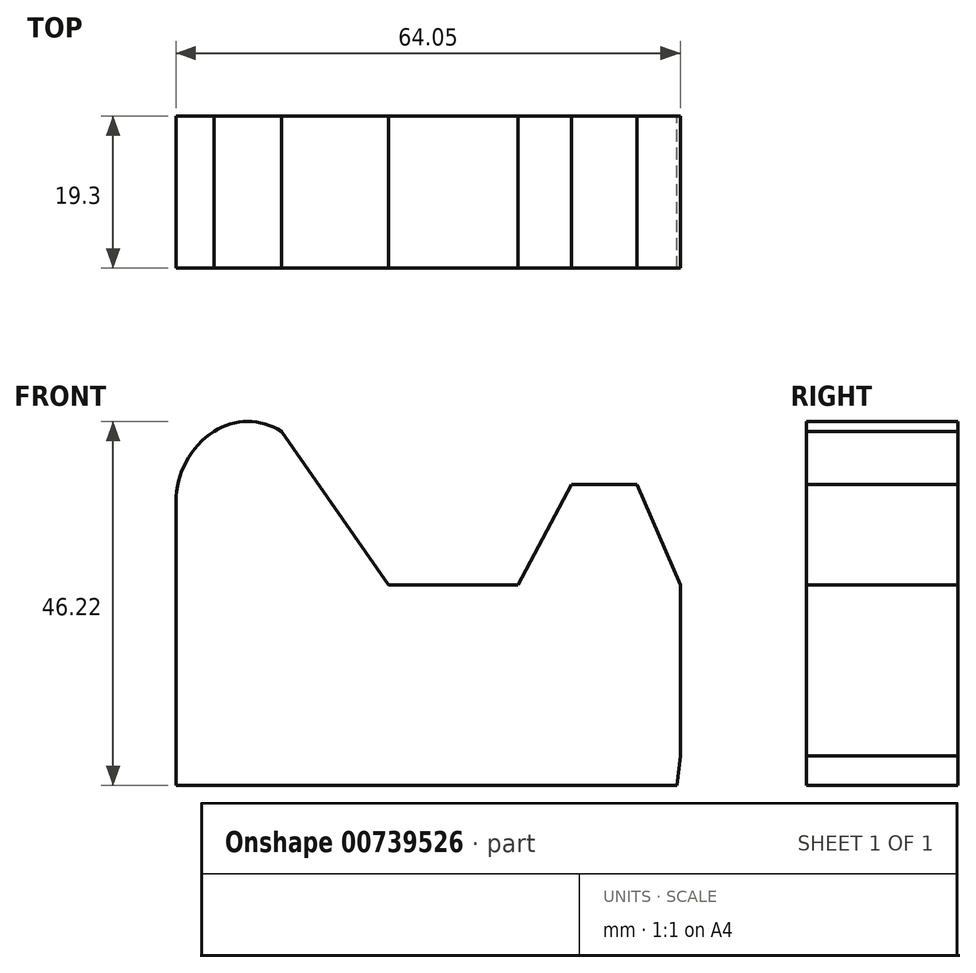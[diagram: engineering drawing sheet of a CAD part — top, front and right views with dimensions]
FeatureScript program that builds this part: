
annotation { "Feature Type Name" : "Feature", "Feature Type Description" : "" }
export const myFeature = defineFeature(function(context is Context, id is Id, definition is map)
    precondition{}
    {
        {
            var Q0;
            Q0=qCreatedBy(makeId("Front.planeOp"),FACE);
            var sketch = newSketch(context, id + "F0", { "sketchPlane" : qUnion([Q0])});
            skLineSegment(sketch, "E0.bottom", {"start": v(-26.99, 1.9) * mm, "end": v(26.99, 1.9) * mm});
            skLineSegment(sketch, "E0.top", {"start": v(-26.99, -1.9) * mm, "end": v(26.99, -1.9) * mm});
            skLineSegment(sketch, "E0.left", {"start": v(-26.99, 1.9) * mm, "end": v(-26.99, -1.9) * mm});
            skPoint(sketch, "E0.middle", {"position": v(0, 0) * mm});
            skLineSegment(sketch, "E1", {"start": v(-26.99, 1.9) * mm, "end": v(-26.99, 34.11) * mm});
            skArc(sketch, "E2", {"start": v(-22.18, 43.08) * mm, "mid": v(-25.7, 39.2) * mm, "end": v(-26.99, 34.11) * mm});
            skArc(sketch, "E3", {"start": v(-13.6, 43.08) * mm, "mid": v(-17.9, 44.32) * mm, "end": v(-22.18, 43.08) * mm});
            skLineSegment(sketch, "E4", {"start": v(-13.6, 43.08) * mm, "end": v(0, 23.58) * mm});
            skLineSegment(sketch, "E5", {"start": v(0, 23.58) * mm, "end": v(16.44, 23.58) * mm});
            skLineSegment(sketch, "E6", {"start": v(16.44, 23.58) * mm, "end": v(23.24, 36.3) * mm});
            skLineSegment(sketch, "E7", {"start": v(23.24, 36.3) * mm, "end": v(31.58, 36.3) * mm});
            skLineSegment(sketch, "E8", {"start": v(31.58, 36.3) * mm, "end": v(37.06, 23.58) * mm});
            skLineSegment(sketch, "E9", {"start": v(37.06, 23.58) * mm, "end": v(37.06, 1.87) * mm});
            skLineSegment(sketch, "E10", {"start": v(37.06, 1.87) * mm, "end": v(26.99, 1.9) * mm});
            skLineSegment(sketch, "E11", {"start": v(26.99, -1.9) * mm, "end": v(36.62, -1.9) * mm});
            skLineSegment(sketch, "E12", {"start": v(36.62, -1.9) * mm, "end": v(37.06, 1.87) * mm});
            skLineSegment(sketch, "E13.top", {"start": v(-26.99, -9.04) * mm, "end": v(26.99, -9.04) * mm});
            skLineSegment(sketch, "E13.left", {"start": v(-26.99, -1.9) * mm, "end": v(-26.99, -9.04) * mm});
            skLineSegment(sketch, "E13.right", {"start": v(26.99, -1.9) * mm, "end": v(26.99, -9.04) * mm});
            skPoint(sketch, "E13.middle", {"position": v(0, -5.47) * mm});
            skLineSegment(sketch, "E14.bottom", {"start": v(-26.99, -3.99) * mm, "end": v(26.99, -3.99) * mm});
            skLineSegment(sketch, "E14.top", {"start": v(-26.99, -6.95) * mm, "end": v(26.99, -6.95) * mm});
            skLineSegment(sketch, "E14.left", {"start": v(-26.99, -3.99) * mm, "end": v(-26.99, -6.95) * mm});
            skLineSegment(sketch, "E14.right", {"start": v(26.99, -3.99) * mm, "end": v(26.99, -6.95) * mm});
            skSolve(sketch);
        }
        {
            var Q0;
            Q0=makeQuery(id+"F0.imprint","IMPRINT",FACE,{"disambiguationData":[TD([[makeQuery(id+"F0.imprint","IMPRINT",EDGE,{"derivedFrom":sQuery(id+"F0.wireOp",EDGE,"E0.bottom")}),1.0]])]});
            var Q1;
            Q1=makeQuery(id+"F0.imprint","IMPRINT",FACE,{"disambiguationData":[TD([[makeQuery(id+"F0.imprint","IMPRINT",EDGE,{"derivedFrom":sQuery(id+"F0.wireOp",EDGE,"E0.bottom")}),-1.0]])]});
            extrude(context, id + "F1", {"entities" : qUnion([Q0, Q1]), "depth" : 19.3 * mm, "offsetDistance" : 25.4 * mm});
        }
        {
            var Q0;
            Q0=sQuery(id+"F0.wireOp",EDGE,"E14.bottom");
            var Q1;
            Q1=sQuery(id+"F0.wireOp",EDGE,"E14.top");
            extrude(context, id + "F2", {"bodyType" : ToolBodyType.SURFACE, "surfaceEntities" : qUnion([Q0, Q1]), "endBound" : BoundingType.SYMMETRIC, "depth" : 58.93 * mm, "offsetDistance" : 25.4 * mm});
        }
    });
